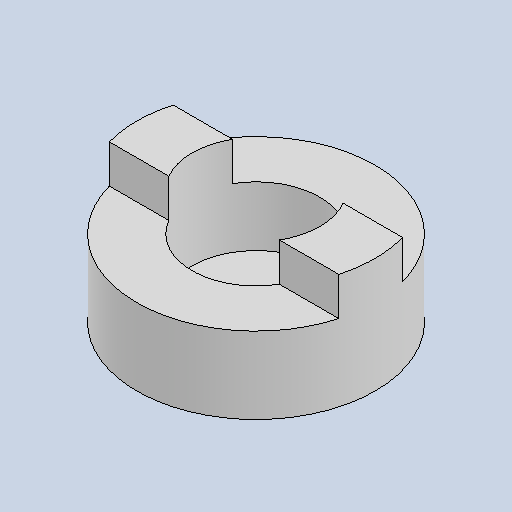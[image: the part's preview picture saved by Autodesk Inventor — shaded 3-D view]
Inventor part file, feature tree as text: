
AUTODESK INVENTOR PART (.ipt)
format: ipt  version: 2022 (Build 260153000, 153)  size: 125,952 bytes
history: native  units: mm
features: sketch x4, extrude x3, hole x1
ambient origin geometry x8: Origin, YZ Plane, XZ Plane, XY Plane, X Axis, Y Axis, Z Axis, Center Point
bodies: Solid1 (feature_tree)
feature tree (8):
  extrude  "Extrusion1"  Depth=15.0mm
  sketch  "Sketch2"  dims[d2=7.0mm d3=0.0mm d4=28.0mm]
  extrude  "Extrusion3"  Depth=7.0mm
  hole  "Hole2"  [1 undecoded]
  extrude  "Extrusion4"  Depth=4.5mm TaperAngle=0.0deg
  sketch  "Sketch1"  dims[d0=28.0mm d1=15.0mm]
  sketch  "Sketch3"  dims[d5=7.5mm d8=2.0mm d9=0.0mm]
  sketch  "Sketch5"  dims[d17=28.0mm d18=4.5mm d19=6.0mm d20=10.59mm d21=3.0mm d22=90.0deg d23=8.0mm d24=20.594885mm d25=4.5mm d26=0.0mm d27=15.0mm d28=28.0mm]
note: 1 required parameter value undecoded (feature->parameter linkage not recoverable at this tier; creation-order binding heuristic only, values carry confidence <= 0.55)
